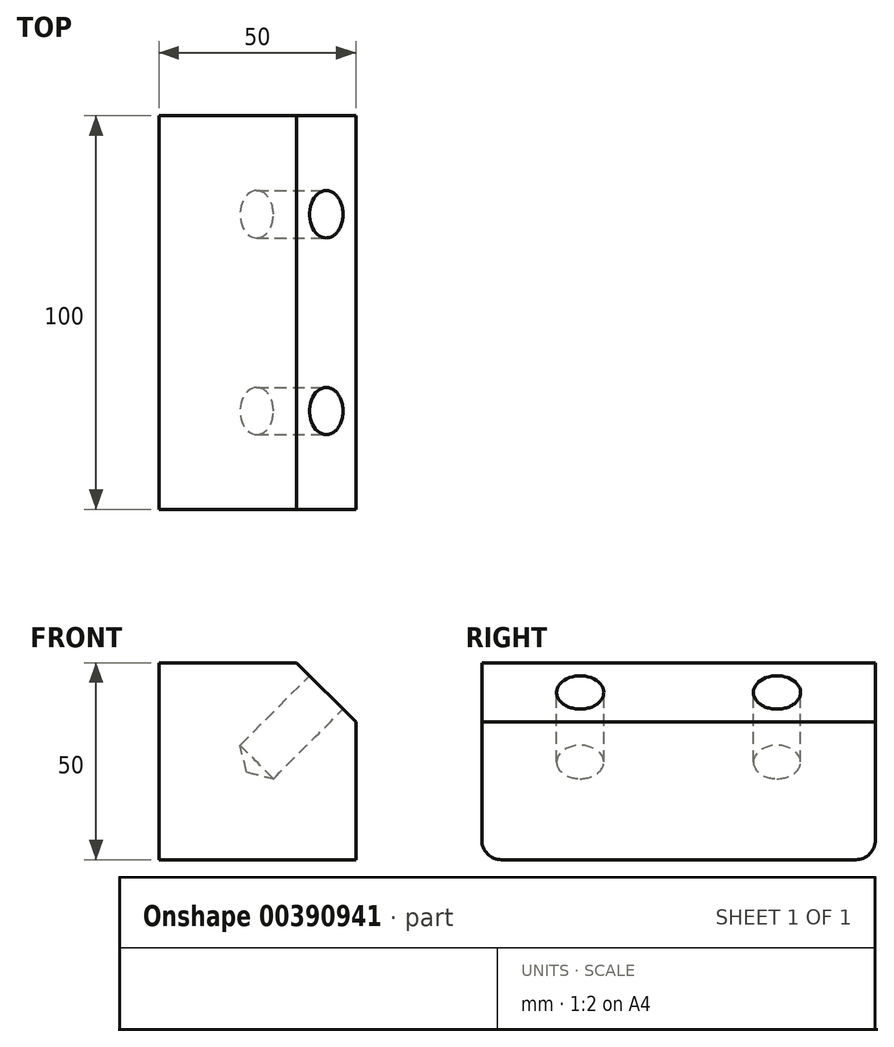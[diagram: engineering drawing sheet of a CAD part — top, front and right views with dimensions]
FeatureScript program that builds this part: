
annotation { "Feature Type Name" : "Feature", "Feature Type Description" : "" }
export const myFeature = defineFeature(function(context is Context, id is Id, definition is map)
    precondition{}
    {
        {
            var Q0;
            Q0=qCreatedBy(makeId("Top.planeOp"),FACE);
            var sketch = newSketch(context, id + "F0", { "sketchPlane" : qUnion([Q0])});
            skLineSegment(sketch, "E0.bottom", {"start": v(0, 0) * mm, "end": v(50, 0) * mm});
            skLineSegment(sketch, "E0.top", {"start": v(0, 100) * mm, "end": v(50, 100) * mm});
            skLineSegment(sketch, "E0.left", {"start": v(0, 0) * mm, "end": v(0, 100) * mm});
            skLineSegment(sketch, "E0.right", {"start": v(50, 0) * mm, "end": v(50, 100) * mm});
            skSolve(sketch);
        }
        {
            var Q0;
            Q0=makeQuery(id+"F0.imprint","IMPRINT",FACE,{"disambiguationData":[TD([[makeQuery(id+"F0.imprint","IMPRINT",EDGE,{"derivedFrom":sQuery(id+"F0.wireOp",EDGE,"E0.bottom")}),1.0]])]});
            extrude(context, id + "F1", {"entities" : qUnion([Q0]), "depth" : 50 * mm});
        }
        {
            var Q0;
            Q0=makeQuery(id+"F1.opExtrude","CAP_EDGE",EDGE,{"disambiguationData":[OSD([sQuery(id+"F0.wireOp",EDGE,"E0.right")])],"isStart":false});
            chamfer(context, id + "F2", {"entities" : qUnion([Q0]), "width" : 15 * mm, "tangentPropagation" : true});
        }
        {
            var Q0;
            Q0=makeQuery(id+"F2.opChamfer","BLEND_FACE",FACE,{"disambiguationData":[OSD([sQuery(id+"F0.wireOp",EDGE,"E0.right")])]});
            var sketch = newSketch(context, id + "F3", { "sketchPlane" : qUnion([Q0])});
            skCircle(sketch, "E1", {"center": v(25, 0) * mm, "radius": 7.8 * mm});
            skCircle(sketch, "E2", {"center": v(75, 0) * mm, "radius": 6.5 * mm});
            skSolve(sketch);
        }
        {
            var Q0;
            Q0=sQuery(id+"F3.wireOp",VERTEX,"E1.center");
            var Q1;
            Q1=sQuery(id+"F3.wireOp",VERTEX,"E2.center");
            var Q2;
            Q2=makeQuery(id+"F1.opExtrude","SWEPT_BODY",BODY,{"disambiguationData":[OSD([sQuery(id+"F0.wireOp",EDGE,"E0.bottom"),sQuery(id+"F0.wireOp",EDGE,"E0.top"),sQuery(id+"F0.wireOp",EDGE,"E0.left"),sQuery(id+"F0.wireOp",EDGE,"E0.right")])]});
            hole(context, id + "F4", {"style" : HoleStyle.SIMPLE, "endStyle" : HoleEndStyle.BLIND, "holeDiameter" : 12 * mm, "holeDepth" : 25 * mm, "isTappedThrough" : true, "tappedDepth" : 12 * mm, "tapClearance" : 3, "locations" : qUnion([Q0, Q1]), "scope" : qUnion([Q2])});
        }
        {
            var Q0;
            Q0=makeQuery(id+"F1.opExtrude","CAP_EDGE",EDGE,{"disambiguationData":[OSD([sQuery(id+"F0.wireOp",EDGE,"E0.top")])],"isStart":true});
            var Q1;
            Q1=makeQuery(id+"F1.opExtrude","CAP_EDGE",EDGE,{"disambiguationData":[OSD([sQuery(id+"F0.wireOp",EDGE,"E0.bottom")])],"isStart":true});
            fillet(context, id + "F5", {"entities" : qUnion([Q0, Q1]), "radius" : 5 * mm, "tangentPropagation" : true, "allowEdgeOverflow" : false});
        }
    });
